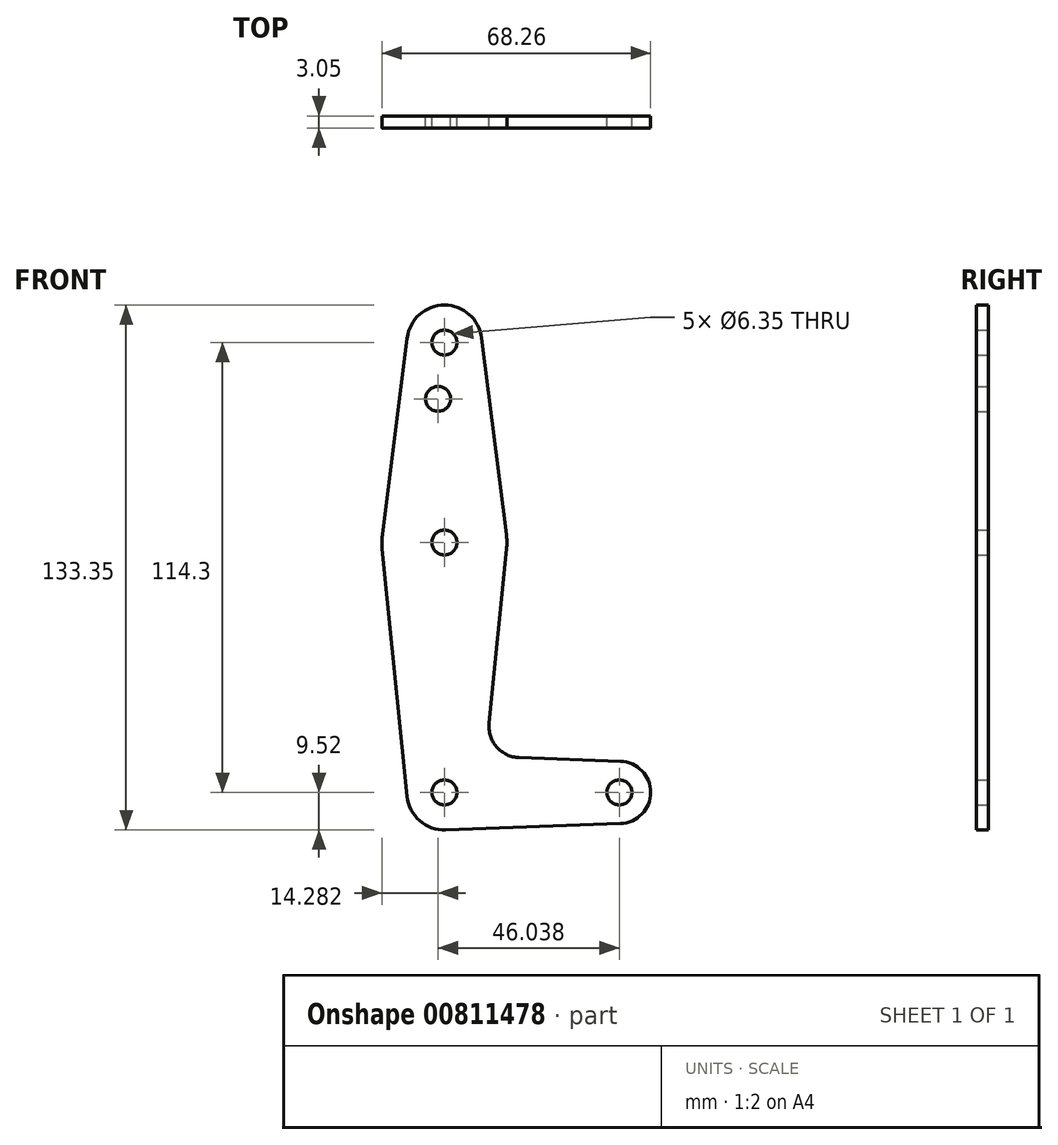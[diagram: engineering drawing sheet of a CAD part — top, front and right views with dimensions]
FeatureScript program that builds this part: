
annotation { "Feature Type Name" : "Feature", "Feature Type Description" : "" }
export const myFeature = defineFeature(function(context is Context, id is Id, definition is map)
    precondition{}
    {
        {
            var Q0;
            Q0=qCreatedBy(makeId("Front.planeOp"),FACE);
            var sketch = newSketch(context, id + "F0", { "sketchPlane" : qUnion([Q0])});
            skLineSegment(sketch, "E0", {"start": v(0, 114.3) * mm, "end": v(0, 0) * mm, "construction": true});
            skLineSegment(sketch, "E1", {"start": v(0, 0) * mm, "end": v(44.45, 0) * mm, "construction": true});
            skCircle(sketch, "E2", {"center": v(0, 114.3) * mm, "radius": 9.53 * mm});
            skCircle(sketch, "E3", {"center": v(0, 63.5) * mm, "radius": 15.88 * mm});
            skCircle(sketch, "E4", {"center": v(0, 0) * mm, "radius": 9.53 * mm});
            skCircle(sketch, "E5", {"center": v(44.45, 0) * mm, "radius": 7.94 * mm});
            skLineSegment(sketch, "E6", {"start": v(44.73, -7.93) * mm, "end": v(0.34, -9.52) * mm});
            skLineSegment(sketch, "E7", {"start": v(-9.45, 115.5) * mm, "end": v(-15.75, 65.48) * mm});
            skLineSegment(sketch, "E8", {"start": v(-15.8, 61.91) * mm, "end": v(-9.48, -0.95) * mm});
            skLineSegment(sketch, "E9", {"start": v(18.97, 8.85) * mm, "end": v(44.73, 7.93) * mm});
            skLineSegment(sketch, "E10", {"start": v(9.45, 115.5) * mm, "end": v(15.75, 65.48) * mm});
            skLineSegment(sketch, "E11", {"start": v(15.8, 61.91) * mm, "end": v(11.34, 17.6) * mm});
            skCircle(sketch, "E12", {"center": v(0, 114.3) * mm, "radius": 3.18 * mm});
            skCircle(sketch, "E13", {"center": v(-1.59, 100) * mm, "radius": 3.18 * mm});
            skCircle(sketch, "E14", {"center": v(0, 63.5) * mm, "radius": 3.18 * mm});
            skCircle(sketch, "E15", {"center": v(0, 0) * mm, "radius": 3.18 * mm});
            skCircle(sketch, "E16", {"center": v(44.45, 0) * mm, "radius": 3.18 * mm});
            skArc(sketch, "E17.filletArc", {"start": v(11.34, 17.6) * mm, "mid": v(13.26, 11.57) * mm, "end": v(18.97, 8.85) * mm});
            skSolve(sketch);
        }
        {
            var Q0;
            Q0=makeQuery(id+"F0.imprint","IMPRINT",FACE,{"disambiguationData":[TD([[makeQuery(id+"F0.imprint","IMPRINT",EDGE,{"derivedFrom":sQuery(id+"F0.wireOp",EDGE,"E12")}),-1.0]])]});
            var Q1;
            {var subQ1=sQuery(id+"F0.wireOp",EDGE,"E7");Q1=makeQuery(id+"F0.imprint","IMPRINT",FACE,{"disambiguationData":[TD([[makeQuery(id+"F0.imprint","IMPRINT",EDGE,{"derivedFrom":subQ1}),1.0]])]});}
            var Q2;
            Q2=makeQuery(id+"F0.imprint","IMPRINT",FACE,{"disambiguationData":[TD([[makeQuery(id+"F0.imprint","IMPRINT",EDGE,{"derivedFrom":sQuery(id+"F0.wireOp",EDGE,"E14")}),-1.0]])]});
            var Q3;
            {var subQ0=sQuery(id+"F0.wireOp",EDGE,"E6");Q3=makeQuery(id+"F0.imprint","IMPRINT",FACE,{"disambiguationData":[TD([[makeQuery(id+"F0.imprint","IMPRINT",EDGE,{"derivedFrom":subQ0}),-1.0]])]});}
            var Q4;
            Q4=makeQuery(id+"F0.imprint","IMPRINT",FACE,{"disambiguationData":[TD([[makeQuery(id+"F0.imprint","IMPRINT",EDGE,{"derivedFrom":sQuery(id+"F0.wireOp",EDGE,"E15")}),-1.0]])]});
            var Q5;
            Q5=makeQuery(id+"F0.imprint","IMPRINT",FACE,{"disambiguationData":[TD([[makeQuery(id+"F0.imprint","IMPRINT",EDGE,{"derivedFrom":sQuery(id+"F0.wireOp",EDGE,"E16")}),-1.0]])]});
            extrude(context, id + "F1", {"entities" : qUnion([Q0, Q1, Q2, Q3, Q4, Q5]), "depth" : 3.05 * mm, "offsetDistance" : 25.4 * mm});
        }
    });
